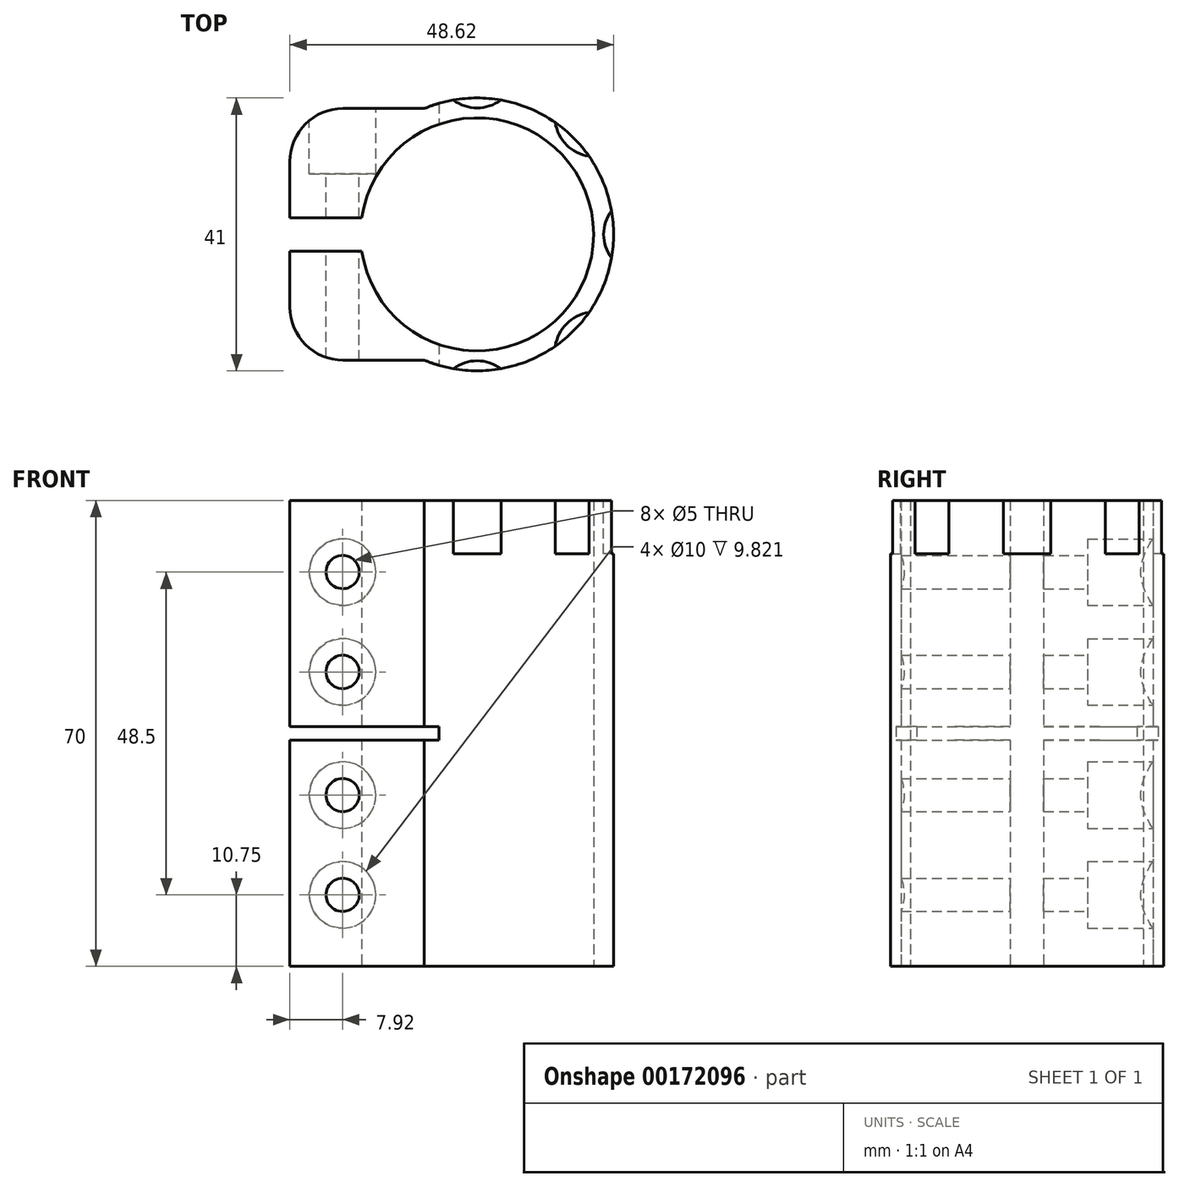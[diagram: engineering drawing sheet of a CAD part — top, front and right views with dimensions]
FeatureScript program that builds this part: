
annotation { "Feature Type Name" : "Feature", "Feature Type Description" : "" }
export const myFeature = defineFeature(function(context is Context, id is Id, definition is map)
    precondition{}
    {
        {
            var Q0;
            Q0=qCreatedBy(makeId("Top.planeOp"),FACE);
            var sketch = newSketch(context, id + "F0", { "sketchPlane" : qUnion([Q0])});
            skArc(sketch, "E0", {"start": v(-17.32, -2.5) * mm, "mid": v(17.5, 0) * mm, "end": v(-17.32, 2.5) * mm});
            skArc(sketch, "E1", {"start": v(-7.92, -18.9) * mm, "mid": v(20.5, 0) * mm, "end": v(-7.92, 18.9) * mm});
            skLineSegment(sketch, "E2", {"start": v(-17.32, 2.5) * mm, "end": v(-28.12, 2.5) * mm});
            skLineSegment(sketch, "E3", {"start": v(-28.12, 2.5) * mm, "end": v(-28.12, 10.9) * mm});
            skLineSegment(sketch, "E4", {"start": v(-20.12, 18.9) * mm, "end": v(-7.92, 18.9) * mm});
            skPoint(sketch, "E5.visualSharp", {"position": v(-28.12, 18.9) * mm});
            skArc(sketch, "E5.filletArc", {"start": v(-20.12, 18.9) * mm, "mid": v(-25.78, 16.57) * mm, "end": v(-28.12, 10.9) * mm});
            skLineSegment(sketch, "E6", {"start": v(0, 0) * mm, "end": v(38.36, 0) * mm, "construction": true});
            skLineSegment(sketch, "E7.MirrorCS", {"start": v(-17.32, -2.5) * mm, "end": v(-28.12, -2.5) * mm});
            skLineSegment(sketch, "E8.MirrorCS", {"start": v(-28.12, -2.5) * mm, "end": v(-28.12, -10.9) * mm});
            skArc(sketch, "E9.MirrorCS", {"start": v(-20.12, -18.9) * mm, "mid": v(-25.78, -16.57) * mm, "end": v(-28.12, -10.9) * mm});
            skLineSegment(sketch, "E10.MirrorCS", {"start": v(-20.12, -18.9) * mm, "end": v(-7.92, -18.9) * mm});
            skSolve(sketch);
        }
        {
            var Q0;
            Q0 = qSketchRegion(id + "F0", true);
            extrude(context, id + "F1", {"entities" : qUnion([Q0]), "endBound" : BoundingType.SYMMETRIC, "depth" : 70 * mm});
        }
        {
            var Q0;
            Q0=makeQuery(id+"F1.opExtrude","SWEPT_FACE",FACE,{"disambiguationData":[OSD([sQuery(id+"F0.wireOp",EDGE,"E4")])]});
            var sketch = newSketch(context, id + "F2", { "sketchPlane" : qUnion([Q0])});
            skPoint(sketch, "E11", {"position": v(20.2, 24.25) * mm});
            skPoint(sketch, "E12", {"position": v(20.2, 9.25) * mm});
            skPoint(sketch, "E13", {"position": v(20.2, -9.25) * mm});
            skPoint(sketch, "E14", {"position": v(20.2, -24.25) * mm});
            skSolve(sketch);
        }
        {
            var Q0;
            Q0=sQuery(id+"F2.wireOp",VERTEX,"E14");
            var Q1;
            Q1=sQuery(id+"F2.wireOp",VERTEX,"E13");
            var Q2;
            Q2=sQuery(id+"F2.wireOp",VERTEX,"E12");
            var Q3;
            Q3=sQuery(id+"F2.wireOp",VERTEX,"E11");
            var Q4;
            Q4=makeQuery(id+"F1.opExtrude","SWEPT_BODY",BODY,{"disambiguationData":[OSD([sQuery(id+"F0.wireOp",EDGE,"E0"),sQuery(id+"F0.wireOp",EDGE,"E1"),sQuery(id+"F0.wireOp",EDGE,"E2"),sQuery(id+"F0.wireOp",EDGE,"E3"),sQuery(id+"F0.wireOp",EDGE,"E4"),sQuery(id+"F0.wireOp",EDGE,"E5.filletArc"),sQuery(id+"F0.wireOp",EDGE,"E7.MirrorCS"),sQuery(id+"F0.wireOp",EDGE,"E8.MirrorCS"),sQuery(id+"F0.wireOp",EDGE,"E9.MirrorCS"),sQuery(id+"F0.wireOp",EDGE,"E10.MirrorCS")])]});
            hole(context, id + "F3", {"style" : HoleStyle.C_BORE, "endStyle" : HoleEndStyle.THROUGH, "holeDiameter" : 5 * mm, "cBoreDiameter" : 10 * mm, "cBoreDepth" : 8 * mm, "locations" : qUnion([Q0, Q1, Q2, Q3]), "scope" : qUnion([Q4]), "isTappedThrough" : true});
        }
        {
            var Q0;
            Q0=qCreatedBy(makeId("Front.planeOp"),FACE);
            var sketch = newSketch(context, id + "F4", { "sketchPlane" : qUnion([Q0])});
            skLineSegment(sketch, "E15.bottom", {"start": v(-28.12, 1) * mm, "end": v(-5.72, 1) * mm});
            skLineSegment(sketch, "E15.top", {"start": v(-28.12, -1) * mm, "end": v(-5.72, -1) * mm});
            skLineSegment(sketch, "E15.left", {"start": v(-28.12, 1) * mm, "end": v(-28.12, -1) * mm});
            skLineSegment(sketch, "E15.right", {"start": v(-5.72, 1) * mm, "end": v(-5.72, -1) * mm});
            skSolve(sketch);
        }
        {
            var Q0;
            Q0 = qSketchRegion(id + "F4", true);
            extrude(context, id + "F5", {"entities" : qUnion([Q0]), "operationType" : NewBodyOperationType.REMOVE, "endBound" : BoundingType.SYMMETRIC, "oppositeDirection" : true, "depth" : 50 * mm});
        }
        {
            var Q0;
            Q0=makeQuery(id+"F1.opExtrude","CAP_FACE",FACE,{"disambiguationData":[OSD([sQuery(id+"F0.wireOp",EDGE,"E0"),sQuery(id+"F0.wireOp",EDGE,"E1"),sQuery(id+"F0.wireOp",EDGE,"E2"),sQuery(id+"F0.wireOp",EDGE,"E3"),sQuery(id+"F0.wireOp",EDGE,"E4"),sQuery(id+"F0.wireOp",EDGE,"E5.filletArc"),sQuery(id+"F0.wireOp",EDGE,"E7.MirrorCS"),sQuery(id+"F0.wireOp",EDGE,"E8.MirrorCS"),sQuery(id+"F0.wireOp",EDGE,"E9.MirrorCS"),sQuery(id+"F0.wireOp",EDGE,"E10.MirrorCS")])],"isStart":false});
            var sketch = newSketch(context, id + "F6", { "sketchPlane" : qUnion([Q0])});
            skCircle(sketch, "E16", {"center": v(0, -25) * mm, "radius": 6 * mm});
            skCircle(sketch, "E17.1.0", {"center": v(17.68, -17.68) * mm, "radius": 6 * mm});
            skCircle(sketch, "E17.2.0", {"center": v(25, 0) * mm, "radius": 6 * mm});
            skCircle(sketch, "E17.3.0", {"center": v(17.68, 17.68) * mm, "radius": 6 * mm});
            skCircle(sketch, "E17.4.0", {"center": v(0, 25) * mm, "radius": 6 * mm});
            skPoint(sketch, "E17.center", {"position": v(0, 0) * mm});
            skLineSegment(sketch, "E17.anchor1", {"start": v(0, 0) * mm, "end": v(0, -25) * mm, "construction": true});
            skLineSegment(sketch, "E17.anchor2", {"start": v(0, 0) * mm, "end": v(0, 25) * mm, "construction": true});
            skSolve(sketch);
        }
        {
            var Q0;
            Q0 = qSketchRegion(id + "F6", true);
            extrude(context, id + "F7", {"entities" : qUnion([Q0]), "operationType" : NewBodyOperationType.REMOVE, "oppositeDirection" : true, "depth" : 8 * mm});
        }
    });
